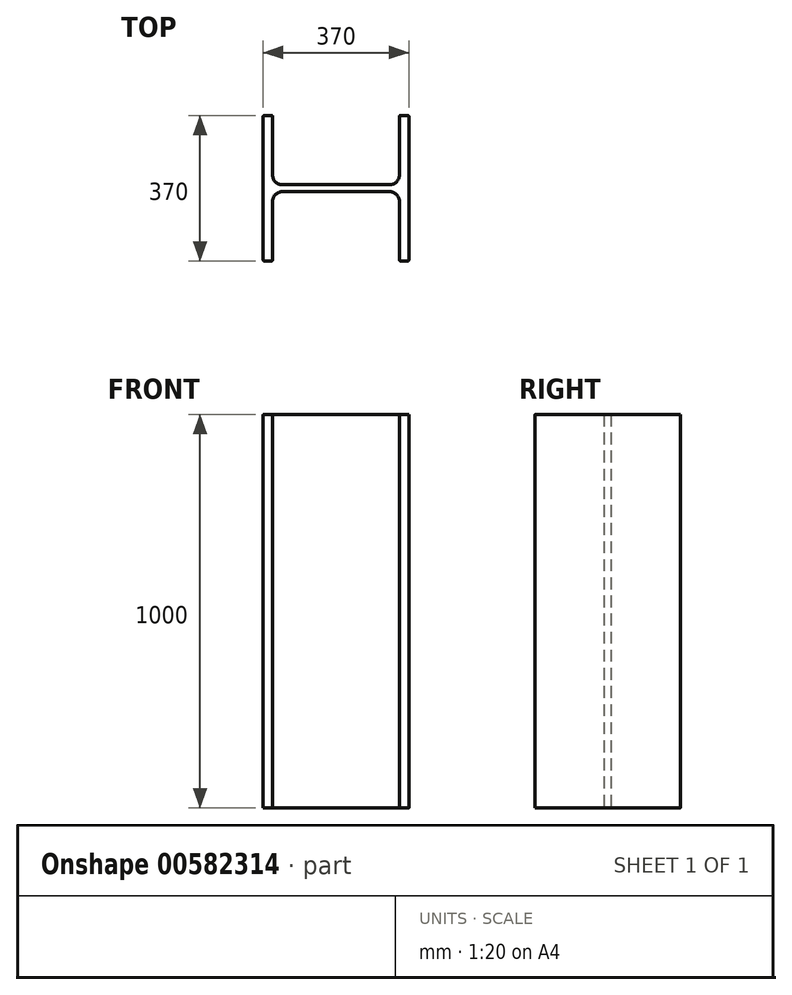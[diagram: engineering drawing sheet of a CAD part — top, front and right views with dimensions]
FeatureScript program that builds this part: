
annotation { "Feature Type Name" : "Feature", "Feature Type Description" : "" }
export const myFeature = defineFeature(function(context is Context, id is Id, definition is map)
    precondition{}
    {
        {
            var Q0;
            Q0=qCreatedBy(makeId("Top.planeOp"),FACE);
            var sketch = newSketch(context, id + "F0", { "sketchPlane" : qUnion([Q0])});
            skLineSegment(sketch, "E0.left", {"start": v(185, 185) * mm, "end": v(185, -185) * mm});
            skLineSegment(sketch, "E0.right", {"start": v(-185, 185) * mm, "end": v(-185, -185) * mm});
            skPoint(sketch, "E0.middle", {"position": v(0, 0) * mm});
            skLineSegment(sketch, "E1", {"start": v(-185, -185) * mm, "end": v(-161, -185) * mm});
            skLineSegment(sketch, "E2", {"start": v(-161, -185) * mm, "end": v(-161, -9) * mm});
            skLineSegment(sketch, "E3", {"start": v(-161, -9) * mm, "end": v(161, -9) * mm});
            skLineSegment(sketch, "E4", {"start": v(161, -9) * mm, "end": v(161, -185) * mm});
            skLineSegment(sketch, "E5", {"start": v(161, -185) * mm, "end": v(185, -185) * mm});
            skLineSegment(sketch, "E6", {"start": v(-185, 185) * mm, "end": v(-161, 185) * mm});
            skLineSegment(sketch, "E7", {"start": v(-161, 185) * mm, "end": v(-161, 9) * mm});
            skLineSegment(sketch, "E8", {"start": v(-161, 9) * mm, "end": v(161, 9) * mm});
            skLineSegment(sketch, "E9", {"start": v(161, 9) * mm, "end": v(161, 185) * mm});
            skLineSegment(sketch, "E10", {"start": v(161, 185) * mm, "end": v(185, 185) * mm});
            skSolve(sketch);
        }
        {
            var Q0;
            Q0 = qSketchRegion(id + "F0", true);
            extrude(context, id + "F1", {"entities" : qUnion([Q0]), "depth" : 1000 * mm, "offsetDistance" : 25 * mm});
        }
        {
            var Q0;
            Q0=makeQuery(id+"F1.opExtrude","SWEPT_EDGE",EDGE,{"disambiguationData":[OSD([sQuery(id+"F0.wireOp",EDGE,"E2"),sQuery(id+"F0.wireOp",EDGE,"E3")])]});
            var Q1;
            Q1=makeQuery(id+"F1.opExtrude","SWEPT_EDGE",EDGE,{"disambiguationData":[OSD([sQuery(id+"F0.wireOp",EDGE,"E3"),sQuery(id+"F0.wireOp",EDGE,"E4")])]});
            var Q2;
            Q2=makeQuery(id+"F1.opExtrude","SWEPT_EDGE",EDGE,{"disambiguationData":[OSD([sQuery(id+"F0.wireOp",EDGE,"E8"),sQuery(id+"F0.wireOp",EDGE,"E9")])]});
            var Q3;
            Q3=makeQuery(id+"F1.opExtrude","SWEPT_EDGE",EDGE,{"disambiguationData":[OSD([sQuery(id+"F0.wireOp",EDGE,"E7"),sQuery(id+"F0.wireOp",EDGE,"E8")])]});
            fillet(context, id + "F2", {"entities" : qUnion([Q0, Q1, Q2, Q3]), "radius" : 24 * mm, "tangentPropagation" : true, "allowEdgeOverflow" : false});
        }
        {
            var Q0;
            Q0=makeQuery(id+"F1.opExtrude","SWEPT_EDGE",EDGE,{"disambiguationData":[OSD([sQuery(id+"F0.wireOp",EDGE,"E9"),sQuery(id+"F0.wireOp",EDGE,"E10")])]});
            var Q1;
            Q1=makeQuery(id+"F1.opExtrude","SWEPT_EDGE",EDGE,{"disambiguationData":[OSD([sQuery(id+"F0.wireOp",EDGE,"E0.left"),sQuery(id+"F0.wireOp",EDGE,"E10")])]});
            var Q2;
            Q2=makeQuery(id+"F1.opExtrude","SWEPT_EDGE",EDGE,{"disambiguationData":[OSD([sQuery(id+"F0.wireOp",EDGE,"E6"),sQuery(id+"F0.wireOp",EDGE,"E7")])]});
            var Q3;
            Q3=makeQuery(id+"F1.opExtrude","SWEPT_EDGE",EDGE,{"disambiguationData":[OSD([sQuery(id+"F0.wireOp",EDGE,"E0.right"),sQuery(id+"F0.wireOp",EDGE,"E6")])]});
            var Q4;
            Q4=makeQuery(id+"F1.opExtrude","SWEPT_EDGE",EDGE,{"disambiguationData":[OSD([sQuery(id+"F0.wireOp",EDGE,"E0.left"),sQuery(id+"F0.wireOp",EDGE,"E5")])]});
            var Q5;
            Q5=makeQuery(id+"F1.opExtrude","SWEPT_EDGE",EDGE,{"disambiguationData":[OSD([sQuery(id+"F0.wireOp",EDGE,"E4"),sQuery(id+"F0.wireOp",EDGE,"E5")])]});
            var Q6;
            Q6=makeQuery(id+"F1.opExtrude","SWEPT_EDGE",EDGE,{"disambiguationData":[OSD([sQuery(id+"F0.wireOp",EDGE,"E0.right"),sQuery(id+"F0.wireOp",EDGE,"E1")])]});
            var Q7;
            Q7=makeQuery(id+"F1.opExtrude","SWEPT_EDGE",EDGE,{"disambiguationData":[OSD([sQuery(id+"F0.wireOp",EDGE,"E1"),sQuery(id+"F0.wireOp",EDGE,"E2")])]});
            fillet(context, id + "F3", {"entities" : qUnion([Q0, Q1, Q2, Q3, Q4, Q5, Q6, Q7]), "radius" : 3 * mm, "tangentPropagation" : true, "allowEdgeOverflow" : false});
        }
    });
